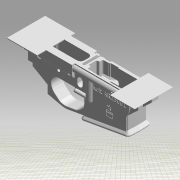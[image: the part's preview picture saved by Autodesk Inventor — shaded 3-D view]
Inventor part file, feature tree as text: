
AUTODESK INVENTOR PART (.ipt)
format: ipt  version: 2018 (Build 220112000, 112)  size: 2,653,184 bytes
history: native  units: mm (DEFAULTED — no unit token found)
features: extrude x23, sketch x23, projected_geometry x10, other x3, fillet x2, reference x1, imported_body x1
ambient origin geometry x8: Origin, YZ Plane, XZ Plane, XY Plane, X Axis, Y Axis, Z Axis, Center Point
bodies: Solid1 (feature_tree)
feature tree (63):
  extrude  "Extrusion1"  Depth=50.8mm TaperAngle=0.0deg
  extrude  "Extrusion2"  Depth=0.508mm TaperAngle=0.0deg
  extrude  "Extrusion3"  Depth=14.097mm
  extrude  "Extrusion4"  Depth=0.508mm TaperAngle=0.0deg
  extrude  "Extrusion5"  Depth=0.508mm TaperAngle=0.0deg
  extrude  "Extrusion6"  Depth=25.4mm TaperAngle=0.0deg
  extrude  "Extrusion7"  Depth=2.54mm TaperAngle=0.0deg
  extrude  "Extrusion8"  Depth=1.016mm TaperAngle=0.0deg
  fillet  "Fillet1"  Radius=1.016mm
  extrude  "Extrusion9"  Depth=1.016mm TaperAngle=0.0deg
  extrude  "Extrusion10"  Depth=0.381mm
  extrude  "Extrusion11"  Depth=0.508mm TaperAngle=0.0deg
  sketch  "Sketch14"  dims[d162=3.0mm d163=25.4mm d164=0.0mm]
  sketch  "Sketch15"  dims[d165=3.0mm d166=25.4mm d167=0.0mm]
  extrude  "Extrusion12"  Depth=25.4mm TaperAngle=0.0deg
  extrude  "Extrusion13"  Depth=25.4mm TaperAngle=0.0deg
  extrude  "Extrusion14"  Depth=76.2mm TaperAngle=0.0deg
  extrude  "Extrusion15"  Depth=76.2mm TaperAngle=0.0deg
  sketch  "Sketch20"  dims[d176=6.3754mm d177=76.2mm d178=0.0mm]
  sketch  "Sketch21"  dims[d179=1.0mm d180=0.0mm d181=1.0mm d182=0.0mm]
  extrude  "Extrusion18"  Depth=76.2mm TaperAngle=0.0deg
  extrude  "Extrusion19"  Depth=1.0mm TaperAngle=0.0deg
  extrude  "Extrusion20"  [1 undecoded]
  extrude  "Extrusion21"  [1 undecoded]
  extrude  "Extrusion22"  [1 undecoded]
  extrude  "Extrusion23"  [1 undecoded]
  extrude  "Extrusion24"  [1 undecoded]
  extrude  "Extrusion25"  [1 undecoded]
  fillet  "Fillet2"  [1 undecoded]
  sketch  "Sketch1"  dims[d0=6.35mm d1=50.8mm d2=0.0mm]
  sketch  "Sketch2"  dims[d3=6.35mm d4=0.508mm d5=0.0mm]
  sketch  "Sketch3"  dims[d6=15.24mm d7=14.097mm]
  sketch  "Sketch5"  dims[d8=0.508mm d9=0.0mm d10=0.508mm d11=0.0mm]
  projected_geometry  "Projected Loop2"
  sketch  "Sketch7"  dims[d12=0.508mm d13=0.0mm d14=0.508mm d15=0.0mm]
  sketch  "Sketch8"  dims[d16=2.54mm d17=0.0mm d18=25.4mm d19=0.0mm]
  sketch  "Sketch9"  dims[d20=1.27mm d21=2.54mm d22=0.0mm]
  projected_geometry  "Projected Loop5"
  sketch  "Sketch10"  dims[d23=1.016mm d24=0.0mm d25=1.016mm d26=0.0mm d27=1.016mm d28=0.0mm]
  projected_geometry  "Projected Loop6"
  projected_geometry  "Projected Loop7"
  sketch  "Sketch11"  dims[d29=1.016mm d30=0.0mm d31=1.016mm d32=0.0mm]
  projected_geometry  "Projected Loop8"
  sketch  "Sketch12"  dims[d48=0.381mm d90=0.635mm d95=0.635mm d96=0.635mm d97=0.635mm d98=0.635mm d99=0.635mm d100=0.635mm d152=0.381mm]
  sketch  "Sketch13"  dims[d153=0.381mm d156=0.508mm d157=0.0mm]
  sketch  "Sketch16"  dims[d168=76.2mm d169=0.0mm d171=76.2mm d172=0.0mm]
  sketch  "Sketch19"  dims[d173=0.127mm d174=76.2mm d175=0.0mm]
  other  "Image4"
  projected_geometry  "Projected Loop10"
  projected_geometry  "Projected Loop11"
  sketch  "Sketch22"  dims[d183=3.175mm]
  reference  "Reference1"
  sketch  "Sketch23"
  projected_geometry  "Projected Loop12"
  sketch  "Sketch24"
  projected_geometry  "Projected Loop13"
  sketch  "Sketch25"
  sketch  "Sketch26"
  sketch  "Sketch27"
  projected_geometry  "Projected Loop14"
  imported_body  "Base1"
  other  "Assembly1"
  other  "FOSSCAD_Lower_Receiver_V5.1gs_buf_tower:1"
note: 7 required parameter values undecoded (feature->parameter linkage not recoverable at this tier; creation-order binding heuristic only, values carry confidence <= 0.55)
